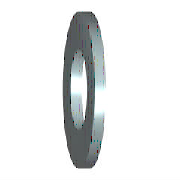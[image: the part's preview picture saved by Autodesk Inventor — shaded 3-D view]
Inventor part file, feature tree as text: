
AUTODESK INVENTOR PART (.ipt)
format: ipt  version: 2024 (Build 280153000, 153)  size: 104,960 bytes
history: native  units: mm (DEFAULTED — no unit token found)
features: other x1, plane x1
ambient origin geometry x7: Origin, YZ Plane, XY Plane, X Axis, Y Axis, Z Axis, Center Point
bodies: Solid1 (feature_tree), Body (feature_tree)
feature tree (2):
  other  "Work Axis1"
  plane  "Work Plane1"
